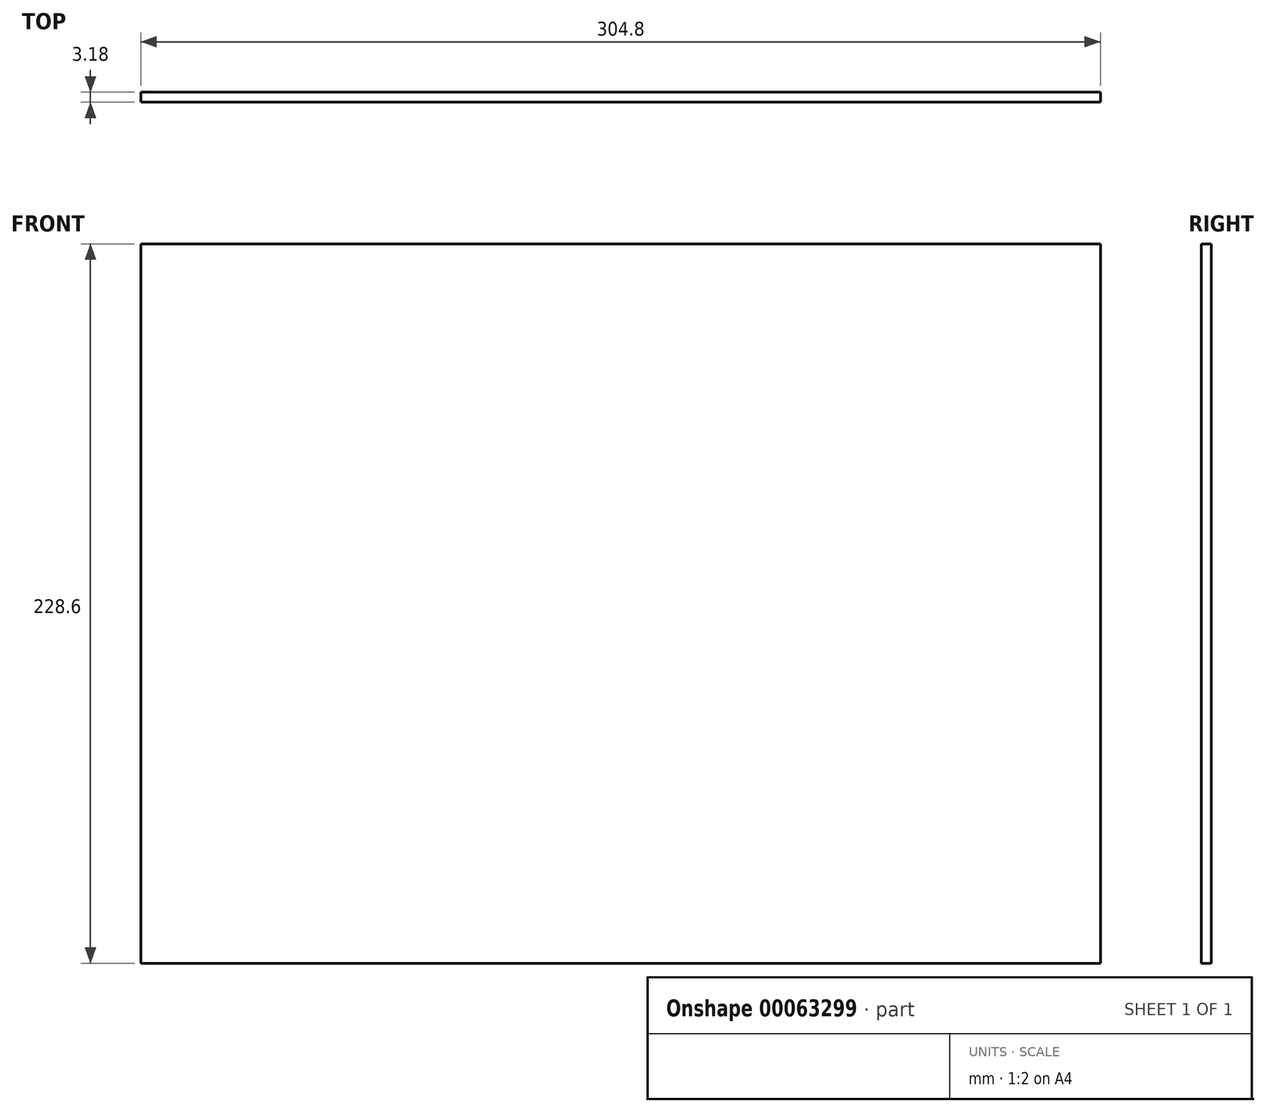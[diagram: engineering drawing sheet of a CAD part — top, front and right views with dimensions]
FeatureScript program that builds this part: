
annotation { "Feature Type Name" : "Feature", "Feature Type Description" : "" }
export const myFeature = defineFeature(function(context is Context, id is Id, definition is map)
    precondition{}
    {
        {
            var Q0;
            Q0=qCreatedBy(makeId("Front.planeOp"),FACE);
            var sketch = newSketch(context, id + "F0", { "sketchPlane" : qUnion([Q0])});
            skLineSegment(sketch, "E0.rect.bottom", {"start": v(152.4, 114.3) * mm, "end": v(-152.4, 114.3) * mm});
            skLineSegment(sketch, "E0.rect.top", {"start": v(152.4, -114.3) * mm, "end": v(-152.4, -114.3) * mm});
            skLineSegment(sketch, "E0.rect.left", {"start": v(152.4, 114.3) * mm, "end": v(152.4, -114.3) * mm});
            skLineSegment(sketch, "E0.rect.right", {"start": v(-152.4, 114.3) * mm, "end": v(-152.4, -114.3) * mm});
            skPoint(sketch, "E0.rect.middle", {"position": v(0, 0) * mm});
            skSolve(sketch);
        }
        {
            var Q0;
            Q0=makeQuery(id+"F0.imprint","IMPRINT",FACE,{"disambiguationData":[TD([[makeQuery(id+"F0.imprint","IMPRINT",EDGE,{"derivedFrom":sQuery(id+"F0.wireOp",EDGE,"E0.rect.bottom")}),1.0]])]});
            extrude(context, id + "F1", {"entities" : qUnion([Q0]), "depth" : 3.17 * mm, "symmetric" : true});
        }
    });
